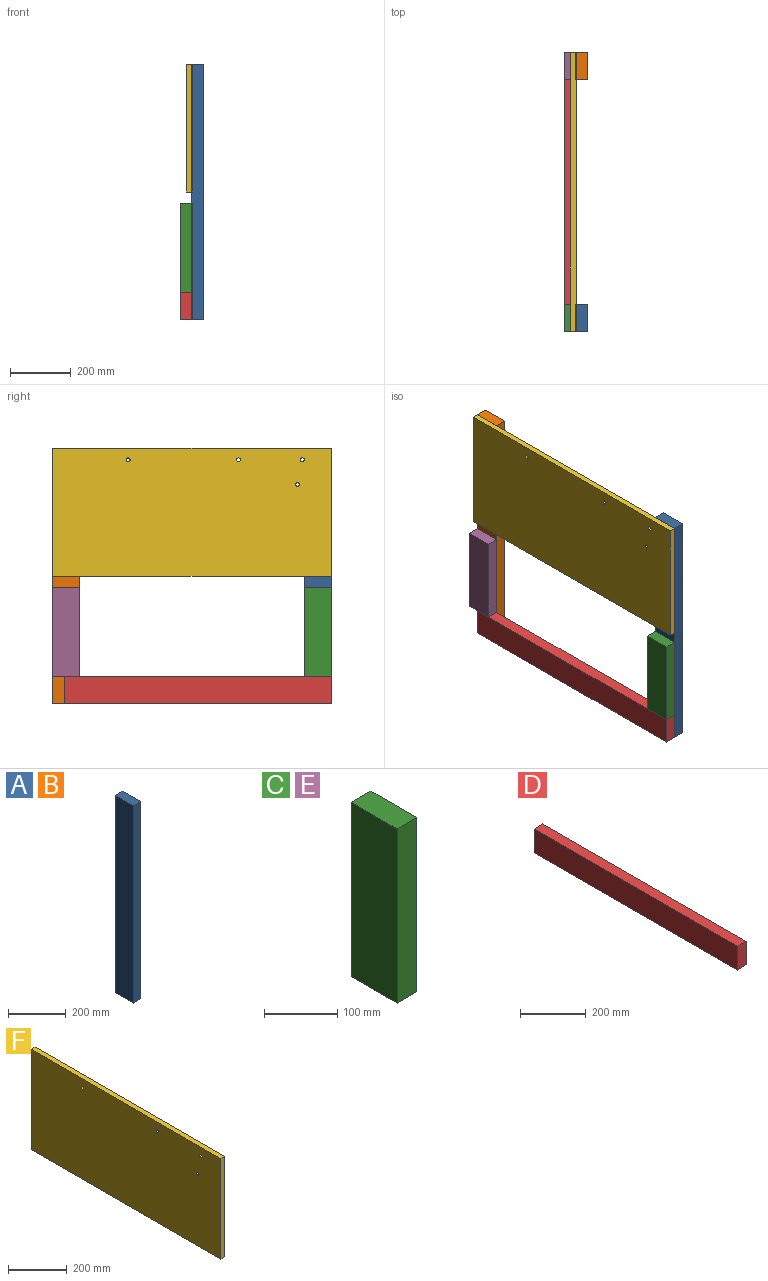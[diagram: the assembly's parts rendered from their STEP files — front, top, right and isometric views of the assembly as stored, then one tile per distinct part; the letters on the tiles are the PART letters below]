
ASSEMBLY  parts=6 mates=16
PART A: 6 faces, bbox 38.1x88.9x838.2 mm
  f0: plane 838.2x88.9mm, normal (-1,0,0), area 74516mm2, adj f1,f3,f4,f5
  f1: plane 838.2x38.1mm, normal (0,-1,0), area 31935.4mm2, adj f0,f2,f4,f5
  f2: plane 838.2x88.9mm, normal (1,0,0), area 74516mm2, adj f1,f3,f4,f5
  f3: plane 838.2x38.1mm, normal (0,1,0), area 31935.4mm2, adj f0,f2,f4,f5
  f4: plane 88.9x38.1mm, normal (0,0,1), area 3387.1mm2, adj f0,f1,f2,f3
  f5: plane 88.9x38.1mm, normal (0,0,-1), area 3387.1mm2, adj f0,f1,f2,f3
PART B: same geometry as A
PART C: 6 faces, bbox 38.1x88.9x292.1 mm
  f0: plane 292.1x38.1mm, normal (0,1,0), area 11129mm2, adj f1,f3,f4,f5
  f1: plane 292.1x88.9mm, normal (-1,0,0), area 25967.7mm2, adj f0,f2,f4,f5
  f2: plane 292.1x38.1mm, normal (0,-1,0), area 11129mm2, adj f1,f3,f4,f5
  f3: plane 292.1x88.9mm, normal (1,0,0), area 25967.7mm2, adj f0,f2,f4,f5
  f4: plane 88.9x38.1mm, normal (0,0,1), area 3387.1mm2, adj f0,f1,f2,f3
  f5: plane 88.9x38.1mm, normal (0,0,-1), area 3387.1mm2, adj f0,f1,f2,f3
PART D: 6 faces, bbox 38.1x876.3x88.9 mm
  f0: plane 876.3x38.1mm, normal (0,0,1), area 33387mm2, adj f1,f3,f4,f5
  f1: plane 876.3x88.9mm, normal (-1,0,0), area 77903.1mm2, adj f0,f2,f4,f5
  f2: plane 876.3x38.1mm, normal (0,0,-1), area 33387mm2, adj f1,f3,f4,f5
  f3: plane 876.3x88.9mm, normal (1,0,0), area 77903.1mm2, adj f0,f2,f4,f5
  f4: plane 88.9x38.1mm, normal (0,1,0), area 3387.1mm2, adj f0,f1,f2,f3
  f5: plane 88.9x38.1mm, normal (0,-1,0), area 3387.1mm2, adj f0,f1,f2,f3
PART E: same geometry as C
PART F: 10 faces, bbox 19.1x914.4x419.1 mm
  f0: plane 914.4x19.05mm, normal (0,0,1), area 17419.3mm2, adj f1,f3,f4,f5
  f1: plane 914.4x419.1mm, normal (-1,0,0), area 382718.3mm2, adj f0,f2,f4,f5,f6,f7,f8,f9
  f2: plane 914.4x19.05mm, normal (0,0,-1), area 17419.3mm2, adj f1,f3,f4,f5
  f3: plane 914.4x419.1mm, normal (1,0,0), area 382718.3mm2, adj f0,f2,f4,f5,f6,f7,f8,f9
  f4: plane 419.1x19.05mm, normal (0,1,0), area 7983.9mm2, adj f0,f1,f2,f3
  f5: plane 419.1x19.05mm, normal (0,-1,0), area 7983.9mm2, adj f0,f1,f2,f3
  f6: cylinder r=6.35mm len=19.05mm, axis (1,0,0), area 760.1mm2, adj f1,f3
  f7: cylinder r=6.35mm len=19.05mm, axis (-1,0,0), area 760.1mm2, adj f1,f3
  f8: cylinder r=6.35mm len=19.05mm, axis (-1,0,0), area 760.1mm2, adj f1,f3
  f9: cylinder r=6.35mm len=19.05mm, axis (-1,0,0), area 760.1mm2, adj f1,f3
PLACE A t=(145.9,-163.16,-347.77)mm
PLACE B t=(145.9,662.34,-347.77)mm
PLACE C t=(85.77,-163.16,-258.87)mm
PLACE D t=(98.4,-252.06,-272.78)mm
PLACE E t=(85.77,662.34,-258.87)mm
PLACE F t=(120.48,-252.06,173.75)mm fixed
MATE planar D.f0 <-> C.f5  axis (0,0,1) through (41.27,186.09,-258.87)mm
MATE planar A.f5 <-> D.f2  axis (0,0,-1) through (79.37,-207.61,-347.77)mm
MATE planar F.f3 <-> A.f0  axis (1,0,0) through (60.32,205.36,280.68)mm
MATE planar A.f1 <-> C.f2  axis (0,-1,0) through (79.37,-252.06,71.33)mm
MATE planar F.f5 <-> A.f1  axis (0,-1,0) through (60.32,-252.06,280.88)mm
MATE planar C.f1 <-> E.f1  axis (-1,0,0) through (22.22,-207.61,-112.82)mm
MATE planar F.f3 <-> B.f0  axis (1,0,0) through (60.32,205.36,280.68)mm
MATE planar A.f1 <-> C.f2  axis (0,-1,0) through (79.37,-252.06,71.33)mm
MATE planar D.f0 <-> E.f5  axis (0,0,1) through (41.27,186.09,-258.87)mm
MATE planar F.f4 <-> B.f3  axis (0,1,0) through (50.8,662.34,280.88)mm
MATE planar B.f3 <-> E.f0  axis (0,1,0) through (79.37,662.34,71.33)mm
MATE planar A.f1 <-> D.f5  axis (0,-1,0) through (79.37,-252.06,71.33)mm
MATE planar F.f0 <-> B.f4  axis (0,0,1) through (50.8,205.14,490.43)mm
MATE planar A.f0 <-> D.f3  axis (-1,0,0) through (60.32,-207.61,71.33)mm
MATE planar F.f0 <-> A.f4  axis (0,0,1) through (50.8,-252.06,490.43)mm
MATE planar A.f0 <-> C.f3  axis (-1,0,0) through (60.32,-252.06,71.33)mm
